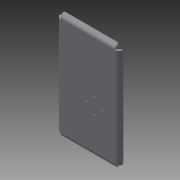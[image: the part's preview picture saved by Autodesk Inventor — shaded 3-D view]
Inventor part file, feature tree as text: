
AUTODESK INVENTOR PART (.ipt)
format: ipt  version: 2013 (Build 170138000, 138)  size: 142,336 bytes
history: native  units: in
note: dims shown in document units (in); Inventor stores cm internally (conversion verified against a paired STEP export)
features: reference x6, sheet_metal_op x4, sketch x2, other x2, chamfer x1
ambient origin geometry x8: Origin, YZ Plane, XZ Plane, XY Plane, X Axis, Y Axis, Z Axis, Center Point
bodies: Solid1 (feature_tree)
feature tree (15):
  sheet_metal_op  "Face1"
  sheet_metal_op  "Flange1"
  chamfer  "Corner Round1"
  sketch  "Sketch1"  dims[d0=2.1654in]
  reference  "Reference1"
  reference  "Reference2"
  reference  "Reference3"
  reference  "Reference4"
  reference  "Reference5"
  reference  "Reference6"
  other  "Plate1"
  sketch  "Sketch2"  dims[d1=3.937in d2=0.0787in d3=0.0787in d4=0.0394in d5=0.1575in d6=0.0787in d7=0.1969in d8=45.0deg d9=0.0787in d10=0.315in d11=0.0787in d12=0.0787in d13=0.0787in]
  other  "Plate2"
  sheet_metal_op  "Bend1"
  sheet_metal_op  "Corner1"
